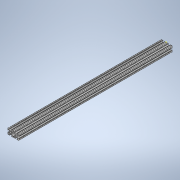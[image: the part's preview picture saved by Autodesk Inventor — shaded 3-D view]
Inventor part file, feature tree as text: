
AUTODESK INVENTOR PART (.ipt)
format: ipt  version: 2020 (Build 240168000, 168)  size: 330,240 bytes
history: native  units: in
note: dims shown in document units (in); Inventor stores cm internally (conversion verified against a paired STEP export)
features: sketch x2, extrude x1
ambient origin geometry x8: Origin, YZ Plane, XZ Plane, XY Plane, X Axis, Y Axis, Z Axis, Center Point
bodies: Solid1 (feature_tree)
feature tree (3):
  extrude  "Extrusion1"  [1 undecoded]
  sketch  "Sketch2"
  sketch  "Sketch1"  dims[d0=27.0in d1=0.0in]
note: 1 required parameter value undecoded (feature->parameter linkage not recoverable at this tier; creation-order binding heuristic only, values carry confidence <= 0.55)
